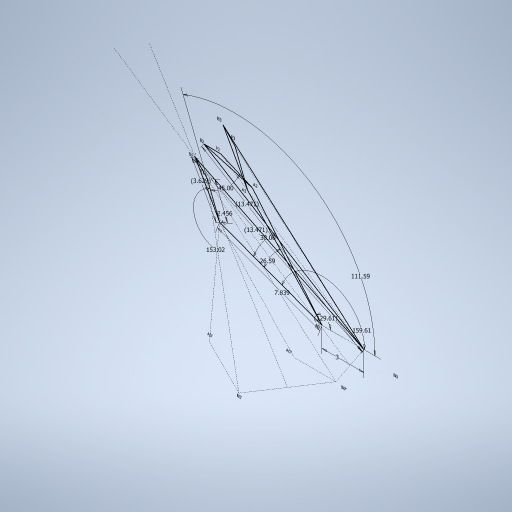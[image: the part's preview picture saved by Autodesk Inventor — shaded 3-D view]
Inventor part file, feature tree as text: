
AUTODESK INVENTOR PART (.ipt)
format: ipt  version: 2024 (Build 280153000, 153)  size: 273,920 bytes
history: native  units: in
note: dims shown in document units (in); Inventor stores cm internally (conversion verified against a paired STEP export)
features: sketch x1
ambient origin geometry x8: Origin, YZ Plane, XZ Plane, XY Plane, X Axis, Y Axis, Z Axis, Center Point
feature tree (1):
  sketch  "Sketch1"  dims[d0=0.3086in d1=0.0967in d2=1.0967in d3=0.7667in d4=30.0deg d5=45.0deg d6=0.1827in d7=1.0515in d9=0.1181in d10=0.5304in d11=0.1429in d12=0.5304in d13=0.8906in]
